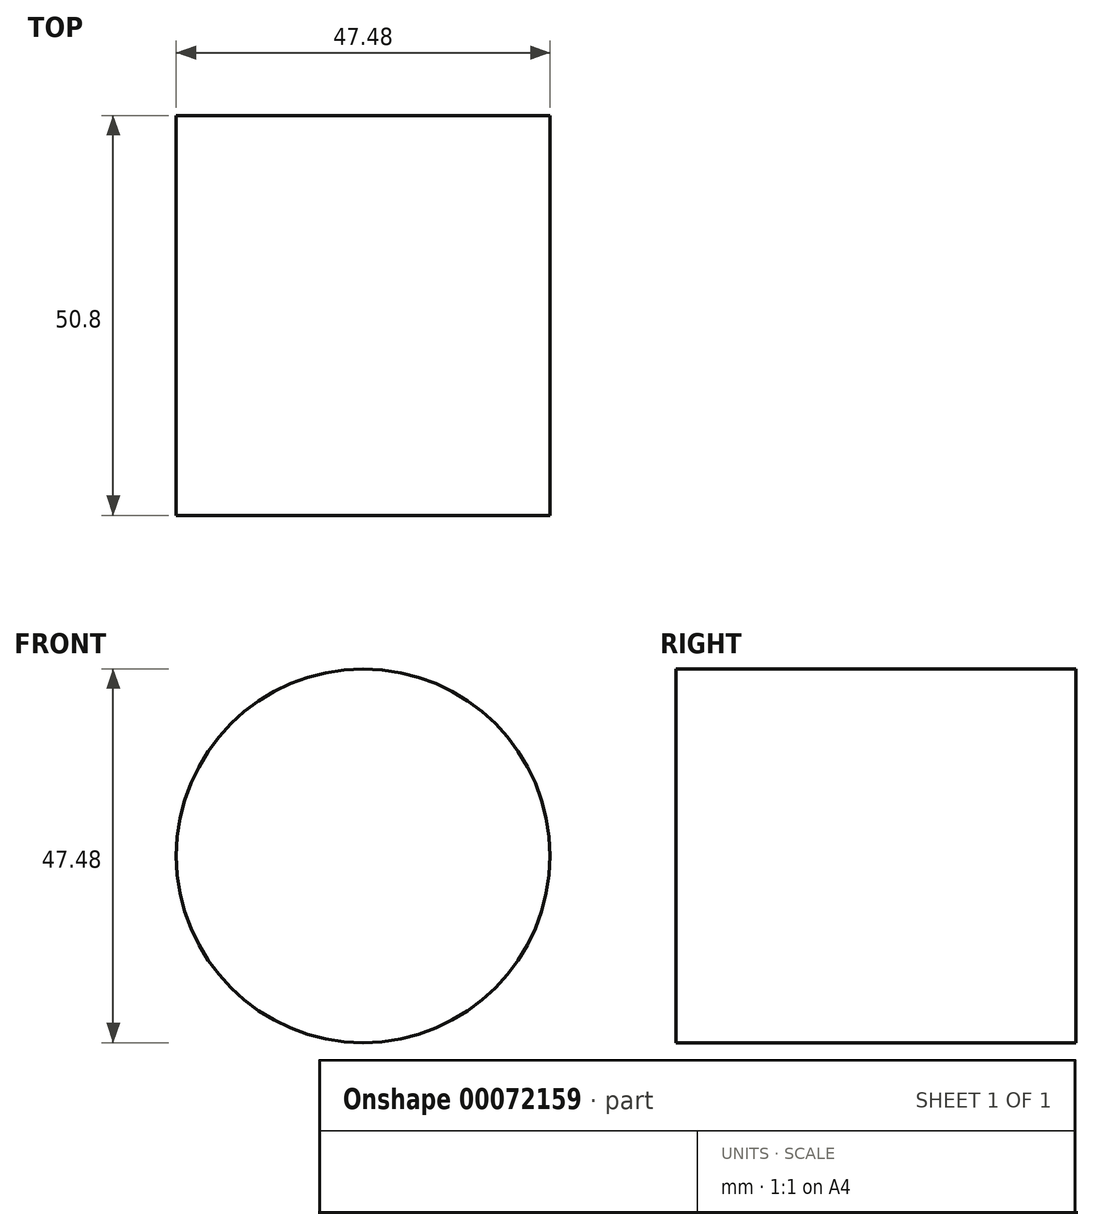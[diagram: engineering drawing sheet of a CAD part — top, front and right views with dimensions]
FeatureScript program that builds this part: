
annotation { "Feature Type Name" : "Feature", "Feature Type Description" : "" }
export const myFeature = defineFeature(function(context is Context, id is Id, definition is map)
    precondition{}
    {
        {
            var Q0;
            Q0=qCreatedBy(makeId("Front.planeOp"),FACE);
            var sketch = newSketch(context, id + "F0", { "sketchPlane" : qUnion([Q0])});
            skCircle(sketch, "E0", {"center": v(0, 0) * mm, "radius": 23.74 * mm});
            skSolve(sketch);
        }
        {
            var Q0;
            Q0 = qSketchRegion(id + "F0", true);
            extrude(context, id + "F1", {"entities" : qUnion([Q0]), "depth" : 50.8 * mm});
        }
    });
